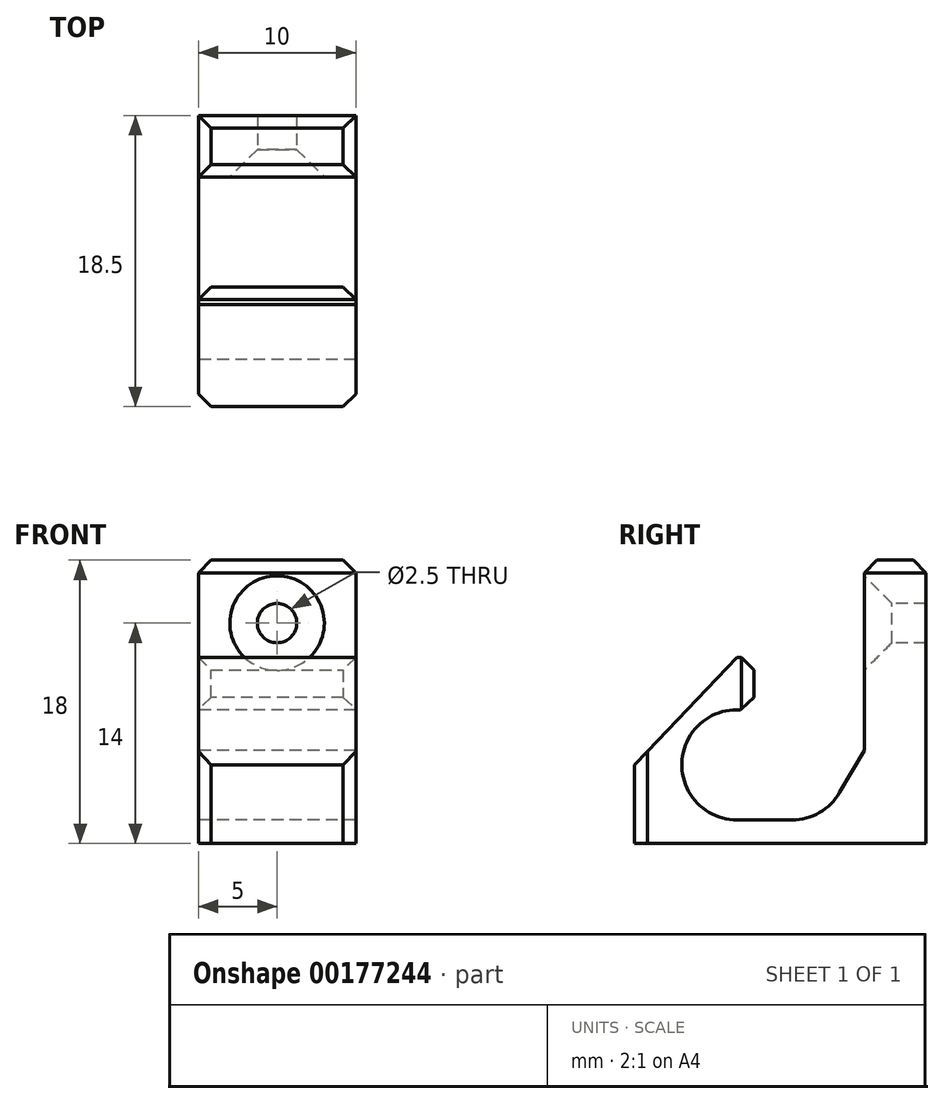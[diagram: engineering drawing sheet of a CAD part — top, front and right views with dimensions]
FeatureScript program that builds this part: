
annotation { "Feature Type Name" : "Feature", "Feature Type Description" : "" }
export const myFeature = defineFeature(function(context is Context, id is Id, definition is map)
    precondition{}
    {
        {
            var Q0;
            Q0=qCreatedBy(makeId("Right.planeOp"),FACE);
            var sketch = newSketch(context, id + "F0", { "sketchPlane" : qUnion([Q0])});
            skLineSegment(sketch, "E0", {"start": v(12, 13) * mm, "end": v(12, -5) * mm});
            skArc(sketch, "E1", {"start": v(1.09, 3.33) * mm, "mid": v(-3.46, 0.55) * mm, "end": v(0, -3.5) * mm});
            skArc(sketch, "E2", {"start": v(3.5, -3.5) * mm, "mid": v(5.24, -3.03) * mm, "end": v(6.52, -1.76) * mm});
            skArc(sketch, "E3", {"start": v(8.09, 3.33) * mm, "mid": v(4.59, 6.83) * mm, "end": v(1.09, 3.33) * mm});
            skLineSegment(sketch, "E4", {"start": v(-3.5, 0) * mm, "end": v(-6.5, 0) * mm});
            skLineSegment(sketch, "E5", {"start": v(-6.5, 0) * mm, "end": v(-6.5, -5) * mm});
            skLineSegment(sketch, "E6", {"start": v(-6.5, -5) * mm, "end": v(12, -5) * mm});
            skLineSegment(sketch, "E7", {"start": v(8.09, 3.33) * mm, "end": v(8.09, 13) * mm});
            skLineSegment(sketch, "E8", {"start": v(8.09, 13) * mm, "end": v(12, 13) * mm});
            skLineSegment(sketch, "E9", {"start": v(1.09, 6.83) * mm, "end": v(0, 6.83) * mm});
            skLineSegment(sketch, "E10", {"start": v(0, 6.83) * mm, "end": v(-6.5, 0) * mm});
            skLineSegment(sketch, "E11", {"start": v(1.09, 3.33) * mm, "end": v(1.09, 6.83) * mm});
            skPoint(sketch, "E12.orphan", {"position": v(4.59, 6.83) * mm});
            skLineSegment(sketch, "E13", {"start": v(3.5, -3.5) * mm, "end": v(0, -3.5) * mm});
            skLineSegment(sketch, "E14", {"start": v(8.09, 3.33) * mm, "end": v(8.09, 0.93) * mm});
            skLineSegment(sketch, "E15", {"start": v(8.09, 0.93) * mm, "end": v(6.52, -1.76) * mm});
            skSolve(sketch);
        }
        {
            var Q0;
            Q0=makeQuery(id+"F0.imprint","IMPRINT",FACE,{"disambiguationData":[TD([[makeQuery(id+"F0.imprint","IMPRINT",EDGE,{"derivedFrom":sQuery(id+"F0.wireOp",EDGE,"E0")}),-1.0]])]});
            var Q1;
            Q1=makeQuery(id+"F0.imprint","IMPRINT",FACE,{"disambiguationData":[TD([[makeQuery(id+"F0.imprint","IMPRINT",EDGE,{"derivedFrom":sQuery(id+"F0.wireOp",EDGE,"E0")}),-1.0]])]});
            var Q2;
            {var subQ0=sQuery(id+"F0.wireOp",EDGE,"E4");Q2=makeQuery(id+"F0.imprint","IMPRINT",FACE,{"disambiguationData":[TD([[makeQuery(id+"F0.imprint","IMPRINT",EDGE,{"derivedFrom":subQ0}),-1.0]])]});}
            extrude(context, id + "F1", {"entities" : qUnion([Q0, Q1, Q2]), "depth" : 10 * mm});
        }
        {
            var Q0;
            Q0=makeQuery(id+"F1.opExtrude","SWEPT_FACE",FACE,{"disambiguationData":[OSD([sQuery(id+"F0.wireOp",EDGE,"E7"),sQuery(id+"F0.wireOp",EDGE,"E14")])]});
            var sketch = newSketch(context, id + "F2", { "sketchPlane" : qUnion([Q0])});
            skLineSegment(sketch, "E16", {"start": v(5, 13) * mm, "end": v(5, 9) * mm});
            skSolve(sketch);
        }
        {
            var Q0;
            Q0=sQuery(id+"F2.wireOp",VERTEX,"E16.end");
            var Q1;
            Q1=makeQuery(id+"F1.opExtrude","SWEPT_BODY",BODY,{"disambiguationData":[OSD([sQuery(id+"F0.wireOp",EDGE,"E0"),sQuery(id+"F0.wireOp",EDGE,"E1"),sQuery(id+"F0.wireOp",EDGE,"E2"),sQuery(id+"F0.wireOp",EDGE,"E5"),sQuery(id+"F0.wireOp",EDGE,"E6"),sQuery(id+"F0.wireOp",EDGE,"E7"),sQuery(id+"F0.wireOp",EDGE,"E8"),sQuery(id+"F0.wireOp",EDGE,"E9"),sQuery(id+"F0.wireOp",EDGE,"E10"),sQuery(id+"F0.wireOp",EDGE,"E11"),sQuery(id+"F0.wireOp",EDGE,"E13"),sQuery(id+"F0.wireOp",EDGE,"E14"),sQuery(id+"F0.wireOp",EDGE,"E15")])]});
            hole(context, id + "F3", {"style" : HoleStyle.C_SINK, "endStyle" : HoleEndStyle.THROUGH, "holeDiameter" : 2.5 * mm, "cSinkDiameter" : 6 * mm, "cSinkAngle" : 90 * degree, "locations" : qUnion([Q0]), "scope" : qUnion([Q1]), "isTappedThrough" : true});
        }
        {
            var Q0;
            Q0=makeQuery(id+"F1.opExtrude","CAP_EDGE",EDGE,{"disambiguationData":[OSD([sQuery(id+"F0.wireOp",EDGE,"E5")])],"isStart":false});
            var Q1;
            Q1=makeQuery(id+"F1.opExtrude","CAP_EDGE",EDGE,{"disambiguationData":[OSD([sQuery(id+"F0.wireOp",EDGE,"E5")])],"isStart":true});
            var Q2;
            Q2=makeQuery(id+"F1.opExtrude","CAP_EDGE",EDGE,{"disambiguationData":[OSD([sQuery(id+"F0.wireOp",EDGE,"E11")])],"isStart":false});
            var Q3;
            Q3=makeQuery(id+"F1.opExtrude","SWEPT_FACE",FACE,{"disambiguationData":[OSD([sQuery(id+"F0.wireOp",EDGE,"E11")])]});
            var Q4;
            Q4=makeQuery(id+"F1.opExtrude","CAP_EDGE",EDGE,{"disambiguationData":[OSD([sQuery(id+"F0.wireOp",EDGE,"E8")])],"isStart":false});
            var Q5;
            Q5=makeQuery(id+"F1.opExtrude","SWEPT_FACE",FACE,{"disambiguationData":[OSD([sQuery(id+"F0.wireOp",EDGE,"E8")])]});
            chamfer(context, id + "F4", {"entities" : qUnion([Q0, Q1, Q2, Q3, Q4, Q5]), "width" : .8 * mm, "tangentPropagation" : true});
        }
    });
